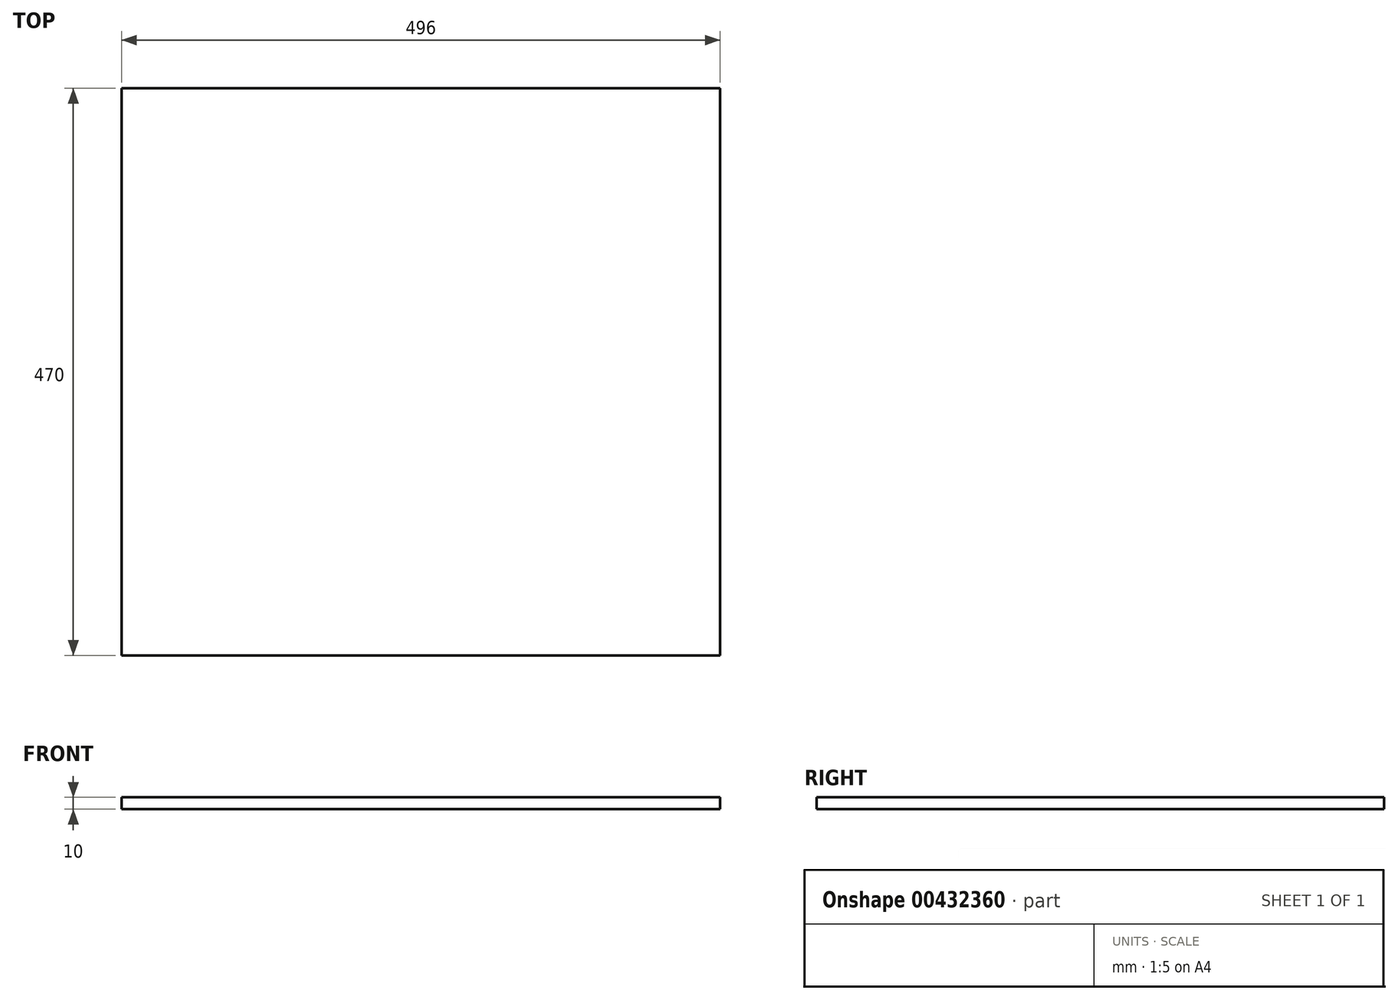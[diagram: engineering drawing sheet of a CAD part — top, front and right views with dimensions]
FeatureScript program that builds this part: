
annotation { "Feature Type Name" : "Feature", "Feature Type Description" : "" }
export const myFeature = defineFeature(function(context is Context, id is Id, definition is map)
    precondition{}
    {
        {
            var Q0;
            Q0=qCreatedBy(makeId("Top.planeOp"),FACE);
            var sketch = newSketch(context, id + "F0", { "sketchPlane" : qUnion([Q0])});
            skLineSegment(sketch, "E0.bottom", {"start": v(-248, 235) * mm, "end": v(248, 235) * mm});
            skLineSegment(sketch, "E0.top", {"start": v(-248, -235) * mm, "end": v(248, -235) * mm});
            skLineSegment(sketch, "E0.left", {"start": v(-248, 235) * mm, "end": v(-248, -235) * mm});
            skLineSegment(sketch, "E0.right", {"start": v(248, 235) * mm, "end": v(248, -235) * mm});
            skPoint(sketch, "E0.middle", {"position": v(0, 0) * mm});
            skSolve(sketch);
        }
        {
            var Q0;
            Q0 = qSketchRegion(id + "F0", true);
            extrude(context, id + "F1", {"entities" : qUnion([Q0]), "depth" : 10 * mm});
        }
    });
